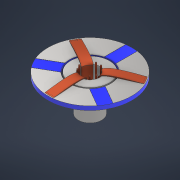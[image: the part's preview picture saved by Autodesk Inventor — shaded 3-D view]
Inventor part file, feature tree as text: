
AUTODESK INVENTOR PART (.ipt)
format: ipt  version: 2021 (Build 250183000, 183)  size: 492,544 bytes
history: native  units: mm
features: other x15, sketch x10, extrude x9, pattern_circular x2
ambient origin geometry x8: Origin, YZ Plane, XZ Plane, XY Plane, X Axis, Y Axis, Z Axis, Center Point
bodies: Body1 (feature_tree)
feature tree (36):
  other  "Contato"
  other  "Sólido1"
  extrude  "Extrusão1"  Depth=6.5mm
  extrude  "Extrusão2"  Depth=3.0mm
  extrude  "Extrusão3"  Depth=0.3mm TaperAngle=0.0deg
  other  "Revolução1"
  other  "Plano de trabalho1"
  extrude  "Extrusão4"  Depth=1.5mm
  extrude  "Extrusão5"  Depth=0.1mm
  pattern_circular  "Padrão circular1"  Count=3 Angle=360.0deg
  other  "Plano de trabalho2"
  extrude  "Extrusão6"  Depth=3.5mm TaperAngle=0.0deg
  extrude  "Extrusão7"  Depth=0.1mm
  pattern_circular  "Padrão circular2"  [2 undecoded]
  other  "Plano de trabalho3"
  extrude  "Extrusão8"  Depth=30.0mm TaperAngle=360.0deg
  extrude  "Extrusão9"  Depth=1.5mm TaperAngle=0.0deg
  sketch  "Esboço1"  dims[d0=1.5mm d1=6.5mm]
  sketch  "Esboço2"  dims[d2=0.3mm d3=0.0mm d4=3.0mm]
  sketch  "Esboço3"  dims[d5=3.2mm d6=0.3mm d7=0.0mm]
  sketch  "Esboço4"  dims[d8=1.8mm d9=1.5mm]
  sketch  "Esboço5"  dims[d10=2.5mm d11=0.0mm d12=0.1mm]
  other  "Contorno projetado1"
  sketch  "Esboço6"  dims[d13=0.1mm]
  other  "Contorno projetado2"
  sketch  "Esboço7"  dims[d14=90.0deg]
  other  "Contorno projetado3"
  other  "Contorno projetado4"
  other  "Contorno projetado5"
  sketch  "Esboço8"  dims[d15=180.0deg]
  sketch  "Esboço9"  dims[d17=0.25mm d18=0.0mm]
  other  "Contorno projetado6"
  other  "Contorno projetado7"
  other  "Contorno projetado8"
  sketch  "Esboço10"  dims[d19=3.5mm d20=0.0mm d21=30.0mm d22=360.0deg d24=3.5mm d25=0.0mm d26=0.1mm d27=3.0mm d28=0.0mm d29=30.0mm d30=360.0deg d32=1.5mm d33=0.0mm d35=0.01mm d36=0.0mm d37=30.0mm d39=360.0deg]
  other  "Contorno projetado9"
note: 2 required parameter values undecoded (feature->parameter linkage not recoverable at this tier; creation-order binding heuristic only, values carry confidence <= 0.55)
